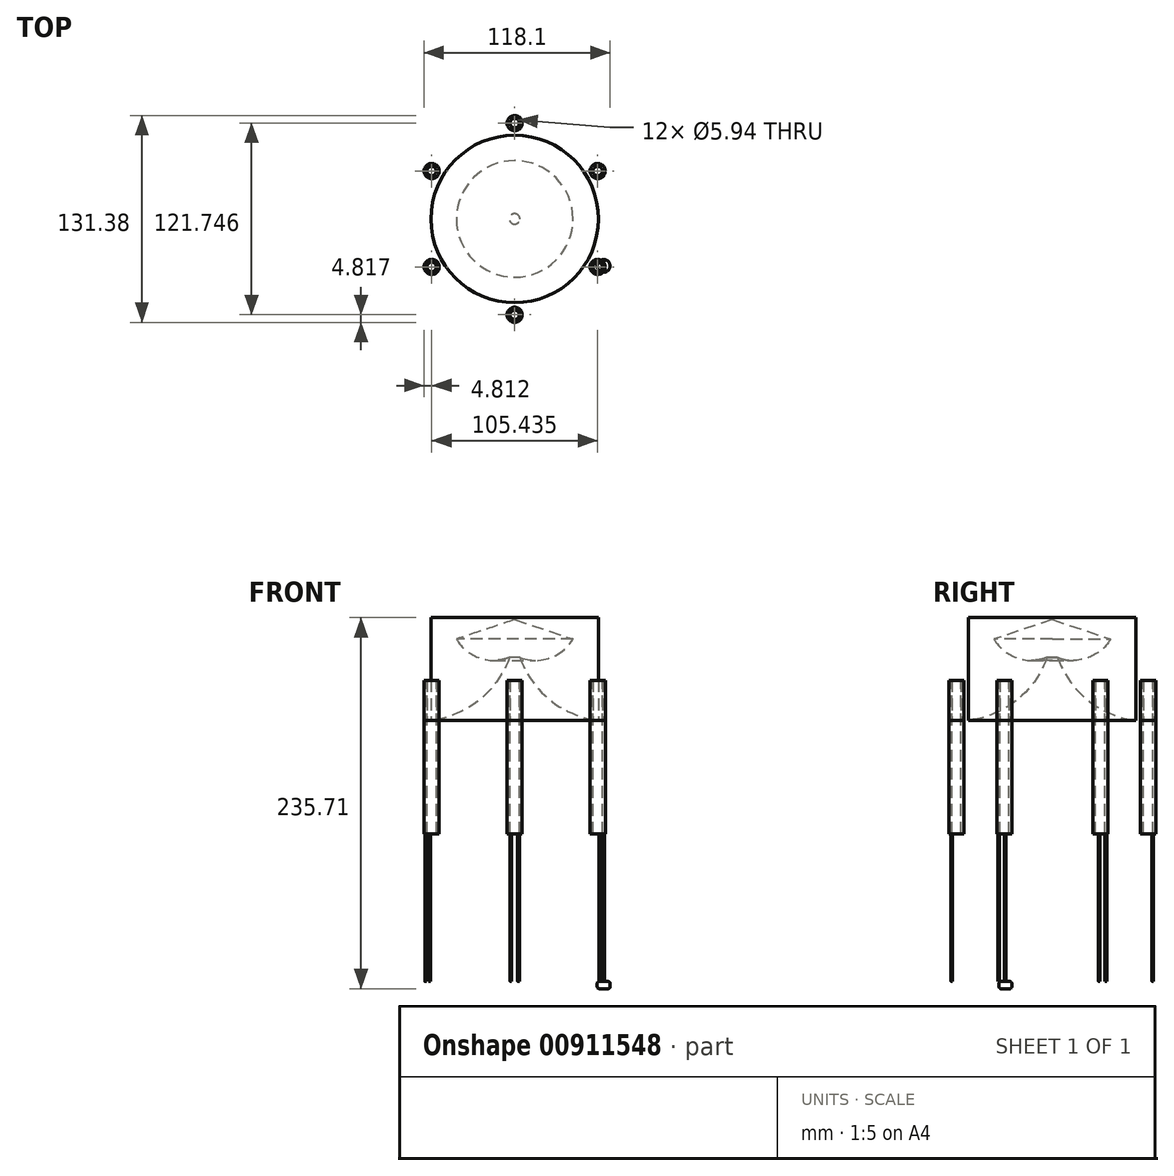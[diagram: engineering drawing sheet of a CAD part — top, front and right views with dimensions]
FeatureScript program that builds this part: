
annotation { "Feature Type Name" : "Feature", "Feature Type Description" : "" }
export const myFeature = defineFeature(function(context is Context, id is Id, definition is map)
    precondition{}
    {
        {
            var Q0;
            Q0=qCreatedBy(makeId("Front.planeOp"),FACE);
            var sketch = newSketch(context, id + "F0", { "sketchPlane" : qUnion([Q0])});
            skArc(sketch, "E0", {"start": v(-67.73, 0) * mm, "mid": v(-18.87, 16.09) * mm, "end": v(0, 63.94) * mm});
            skLineSegment(sketch, "E1", {"start": v(0, 63.94) * mm, "end": v(0, 0) * mm});
            skLineSegment(sketch, "E2", {"start": v(0, 0) * mm, "end": v(-67.73, 0) * mm});
            skArc(sketch, "E3", {"start": v(-37.01, 51.67) * mm, "mid": v(-22.33, 39.61) * mm, "end": v(-3.34, 39.96) * mm});
            skLineSegment(sketch, "E4", {"start": v(0, 63.94) * mm, "end": v(-37.01, 51.67) * mm});
            skSolve(sketch);
        }
        {
            var Q0;
            {var subQ0=sQuery(id+"F0.wireOp",EDGE,"E2");var subQ1=sQuery(id+"F0.wireOp",EDGE,"E0");var subQ2=makeQuery(id+"F0.imprint","INTERSECT",VERTEX,{"disambiguationData":[OD(0.0)],"derivedFrom":[subQ1,subQ0]});Q0=makeQuery(id+"F0.imprint","IMPRINT",FACE,{"disambiguationData":[TD([[makeQuery(id+"F0.imprint","IMPRINT",EDGE,{"disambiguationData":[TD([[subQ2,-1.0]])],"derivedFrom":subQ1}),1.0]])]});}
            var Q1;
            {var subQ0=sQuery(id+"F0.wireOp",EDGE,"E1");Q1=makeQuery(id+"F0.imprint","IMPRINT",FACE,{"disambiguationData":[TD([[makeQuery(id+"F0.imprint","IMPRINT",EDGE,{"derivedFrom":subQ0}),-1.0]])]});}
            var Q2;
            Q2=sQuery(id+"F0.wireOp",EDGE,"E1");
            revolve(context, id + "F1", {"surfaceOperationType" : NewSurfaceOperationType.NEW, "entities" : qUnion([Q0, Q1]), "axis" : qUnion([Q2]), "revolveType" : RevolveType.FULL});
        }
        {
            var Q0;
            Q0=qCreatedBy(makeId("Top.planeOp"),FACE);
            var sketch = newSketch(context, id + "F2", { "sketchPlane" : qUnion([Q0])});
            skCircle(sketch, "E5", {"center": v(0, 60.87) * mm, "radius": 4.81 * mm});
            skCircle(sketch, "E6", {"center": v(0, 60.87) * mm, "radius": 2.97 * mm});
            skCircle(sketch, "E7.1.0", {"center": v(-52.72, 30.44) * mm, "radius": 4.81 * mm});
            skCircle(sketch, "E7.1.1", {"center": v(-52.72, 30.44) * mm, "radius": 2.97 * mm});
            skCircle(sketch, "E7.2.0", {"center": v(-52.72, -30.44) * mm, "radius": 4.81 * mm});
            skCircle(sketch, "E7.2.1", {"center": v(-52.72, -30.44) * mm, "radius": 2.97 * mm});
            skCircle(sketch, "E7.3.0", {"center": v(0, -60.87) * mm, "radius": 4.81 * mm});
            skCircle(sketch, "E7.3.1", {"center": v(0, -60.87) * mm, "radius": 2.97 * mm});
            skCircle(sketch, "E7.4.0", {"center": v(52.72, -30.44) * mm, "radius": 4.81 * mm});
            skCircle(sketch, "E7.4.1", {"center": v(52.72, -30.44) * mm, "radius": 2.97 * mm});
            skCircle(sketch, "E7.5.0", {"center": v(52.72, 30.44) * mm, "radius": 4.81 * mm});
            skCircle(sketch, "E7.5.1", {"center": v(52.72, 30.44) * mm, "radius": 2.97 * mm});
            skPoint(sketch, "E7.center", {"position": v(0, 0) * mm});
            skSolve(sketch);
        }
        {
            var Q0;
            Q0 = qSketchRegion(id + "F2", true);
            extrude(context, id + "F3", {"entities" : qUnion([Q0]), "operationType" : NewBodyOperationType.ADD, "depth" : 25.4 * mm, "offsetDistance" : 25.4 * mm});
        }
        {
            var Q0;
            Q0=makeQuery(id+"F3.opExtrude","CAP_FACE",FACE,{"disambiguationData":[OSD([sQuery(id+"F2.wireOp",EDGE,"E5"),sQuery(id+"F2.wireOp",EDGE,"E6")])],"isStart":false});
            var Q1;
            Q1=makeQuery(id+"F3.opExtrude","CAP_FACE",FACE,{"disambiguationData":[OSD([sQuery(id+"F2.wireOp",EDGE,"E7.5.0"),sQuery(id+"F2.wireOp",EDGE,"E7.5.1")])],"isStart":false});
            var Q2;
            Q2=makeQuery(id+"F3.opExtrude","CAP_FACE",FACE,{"disambiguationData":[OSD([sQuery(id+"F2.wireOp",EDGE,"E7.4.0"),sQuery(id+"F2.wireOp",EDGE,"E7.4.1")])],"isStart":false});
            var Q3;
            Q3=makeQuery(id+"F3.opExtrude","CAP_FACE",FACE,{"disambiguationData":[OSD([sQuery(id+"F2.wireOp",EDGE,"E7.3.0"),sQuery(id+"F2.wireOp",EDGE,"E7.3.1")])],"isStart":false});
            var Q4;
            Q4=makeQuery(id+"F3.opExtrude","CAP_FACE",FACE,{"disambiguationData":[OSD([sQuery(id+"F2.wireOp",EDGE,"E7.2.0"),sQuery(id+"F2.wireOp",EDGE,"E7.2.1")])],"isStart":false});
            var Q5;
            Q5=makeQuery(id+"F3.opExtrude","CAP_FACE",FACE,{"disambiguationData":[OSD([sQuery(id+"F2.wireOp",EDGE,"E7.1.0"),sQuery(id+"F2.wireOp",EDGE,"E7.1.1")])],"isStart":false});
            extrude(context, id + "F4", {"entities" : qUnion([Q0, Q1, Q2, Q3, Q4, Q5]), "oppositeDirection" : true, "depth" : 97.54 * mm, "offsetDistance" : 25.4 * mm});
        }
        {
            var Q0;
            Q0=makeQuery(id+"F4.opExtrude","CAP_FACE",FACE,{"disambiguationData":[OSD([sQuery(id+"F2.wireOp",EDGE,"E7.4.0"),sQuery(id+"F2.wireOp",EDGE,"E7.4.1")])],"isStart":false});
            var sketch = newSketch(context, id + "F5", { "sketchPlane" : qUnion([Q0])});
            skCircle(sketch, "E8", {"center": v(56.5, 29.81) * mm, "radius": 0.5 * mm});
            skCircle(sketch, "E9.1.0", {"center": v(2.43, 63.83) * mm, "radius": 0.5 * mm});
            skCircle(sketch, "E9.2.0", {"center": v(-54.07, 34.02) * mm, "radius": 0.5 * mm});
            skCircle(sketch, "E9.3.0", {"center": v(-56.5, -29.81) * mm, "radius": 0.5 * mm});
            skCircle(sketch, "E9.4.0", {"center": v(-2.43, -63.83) * mm, "radius": 0.5 * mm});
            skCircle(sketch, "E9.5.0", {"center": v(54.07, -34.02) * mm, "radius": 0.5 * mm});
            skPoint(sketch, "E9.center", {"position": v(0, 0) * mm});
            skSolve(sketch);
        }
        {
            var Q0;
            Q0 = qSketchRegion(id + "F5", true);
            extrude(context, id + "F6", {"entities" : qUnion([Q0]), "depth" : 93.73 * mm, "offsetDistance" : 25.4 * mm});
        }
        {
            var Q0;
            Q0=makeQuery(id+"F6.opExtrude","CAP_FACE",FACE,{"disambiguationData":[OSD([sQuery(id+"F5.wireOp",EDGE,"E8")])],"isStart":false});
            var sketch = newSketch(context, id + "F7", { "sketchPlane" : qUnion([Q0])});
            skCircle(sketch, "E10", {"center": v(56.5, 29.81) * mm, "radius": 4.08 * mm});
            skSolve(sketch);
        }
        {
            var Q0;
            Q0 = qSketchRegion(id + "F7", true);
            extrude(context, id + "F8", {"entities" : qUnion([Q0]), "operationType" : NewBodyOperationType.ADD, "depth" : 4.57 * mm, "offsetDistance" : 25.4 * mm});
        }
        {
            var Q0;
            Q0=makeQuery(id+"F8.opExtrude","CAP_EDGE",EDGE,{"disambiguationData":[OSD([sQuery(id+"F7.wireOp",EDGE,"E10")])],"isStart":true});
            var Q1;
            Q1=makeQuery(id+"F8.opExtrude","CAP_EDGE",EDGE,{"disambiguationData":[OSD([sQuery(id+"F7.wireOp",EDGE,"E10")])],"isStart":false});
            fillet(context, id + "F9", {"entities" : qUnion([Q0, Q1]), "radius" : 1.27 * mm, "tangentPropagation" : true, "allowEdgeOverflow" : false});
        }
        {
            var Q0;
            {var subQ0=sQuery(id+"F0.wireOp",EDGE,"E2");var subQ1=sQuery(id+"F0.wireOp",EDGE,"E0");var subQ2=makeQuery(id+"F0.imprint","INTERSECT",VERTEX,{"disambiguationData":[OD(0.0)],"derivedFrom":[subQ1,subQ0]});Q0=makeQuery(id+"F3.boolean.opBoolean","SPLIT",FACE,{"disambiguationData":[TD([makeQuery(id+"F3.opExtrude","SWEPT_FACE",FACE,{"disambiguationData":[OSD([sQuery(id+"F2.wireOp",EDGE,"E5")])]})])],"derivedFrom":makeQuery(id+"F1.opRevolve","SWEPT_FACE",FACE,{"disambiguationData":[OSD([subQ0]),TDD([makeQuery(id+"F0.imprint","IMPRINT",EDGE,{"disambiguationData":[TD([[subQ2,1.0]])],"derivedFrom":subQ0})])]})});}
            extrude(context, id + "F10", {"entities" : qUnion([Q0]), "oppositeDirection" : true, "depth" : 65.28 * mm, "offsetDistance" : 25.4 * mm});
        }
    });
